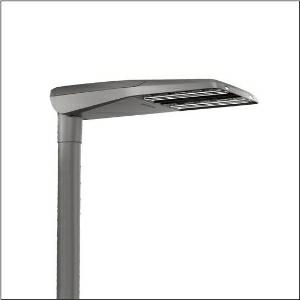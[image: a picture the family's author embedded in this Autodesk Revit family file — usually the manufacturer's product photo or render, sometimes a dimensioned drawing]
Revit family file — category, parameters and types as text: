
# Revit family: streetlight_sl_11_iq_midi___st1_2a_5xc3a51e08le_ac55
name_source: partatom
category: Lighting Fixtures
units: mm (PartAtom-declared; Revit-internal decimal feet)

## family parameters
Cut with Voids When Loaded = No
Host = Face
Light Source = No
Part Type = Normal
Room Calculation Point = No
Round Connector Dimension = Use Diameter
Shared = No

## types (1)
- --- (1 x LED, 9210 lm, 60.4 W, 3000K)
    Apparent Load = 60 VA
    CIE Flux Codes = 32 70 96 100 100
    Color Rendering = 70
    Color Temperature = 3000K
    Default Elevation = 1800 mm
    Description = Streetlight SL 11 iQ midi, mast luminaire, primary light control with 3 zone facetted reflector, of plastic, silver coated, highly specular, primary optical cover: cover, of PMMA, transparent, light distribution: ST1.2a, light emission: direct distribution, primary light characteristic: asymmetric, installation type: post-top, side-entry, lamps: LED, High Power LED, rated values: 9.210lm | 60,4W | 152,5lm/W (begin service life); end service life: 9.210lm | 62,5W; at 50% lumin. flux: 4.605lm | 29,6W | 155,6lm/W, colour temperature: 3000K, colour rendering: CRI > 70, light colour: 730, light setting 1 begin service life: 100% | 9.210lm | 60,4W | 152,5lm/W | 3.000K, light setting 1 end service life: 62,5W, further light settings possible, control: optimised constant luminous flux control (CLO 2.0), Desk-Remote (wireless, voltage-free reading and setting of iQ features in the workshop via application-optimized NFC function/RFID function), Light-Fading, Smart-Wire, Night-Set, Lumen-Switch, Temp-Guard, Auto-Match, with cable H07RN-F 5x 1.5mm², mains connection: 230..240V, AC, 50/60Hz, connection cable pre-assembled, cable length: 8,5m, luminaire housing, of diecast aluminium, powder-coated, Siteco® metallic grey (DB 702S), please order mast flange separately, inclination adjustable without tools: 0°, 5°, 10°, 15° (post-top) | 0°, -5°, -10°, -15° (side-entry), sealing non-destructively replaceable, multi-level sealing system, length: 780mm, width: 376mm, height: 118mm, mast flange for spigot size: 42mm (side-entry): 5XC10008XM4, 60/48mm (side-entry/post-top): 5XC10108XM2, 76/60mm (side-entry/post-top): 5XC10108XM1, equipment: standard, protection rating (complete): IP66, insulation class (complete): insulation class II (safety insulation), certification: CE, ENEC, ENEC+, VDE, impact resistance: IK10, permissible operating ambient temperature for outdoor applications: -25..+50°C, standard-compliant lighting for roads and squares, Environmental Product Declaration (EPD) tested and certified by an independent institute, packaging unit: 1 piece

Light Distribution: ST1.2a
    Height = 118 mm
    Lamp = 1 x LED
    Lamp Light Flux = 9210 lm
    Lamp Power = 60.4 W
    Lamp count = 1
    Length = 780 mm
    Luminous efficacy = 152 lm/W
    Manufacturer = Siteco
    ModVariant = No
    Model = 5XC3A51E08LE
    Number of Poles = 1
    OnlyDefault = Yes
    Power Factor = 1
    Product Name = Streetlight SL 11 iQ midi | ST1.2a
    Product group = mast luminaire | pylon top
    ProductGroupID = 6100
    Protection Class = Protection class II
    Protection Degree = IP 66
    RLX_Detail_Level = 1
    RLX_Emergency_Light_Flux = 0 lm
    RLX_Emergency_Type = 0
    RLX_Emergency_Type_DB = No
    RlxData = <blob elided: 70757 chars, md5=b5577862>
    Socket = socket
    Standby Power = 0 W
    System Light Flux = 9210 lm
    System Power = 60 W
    Type Comments = factory setting: luminous flux: 100 % | dim-lin: 254 | 520 mA
    Type Image = l_1005960.jpg
    URL = http://relux.com
    VarID = @adj_196978
    Voltage = 0 V
    Weight = 0.00 kg
    Width = 376 mm

## geometry (parser evidence)
native form markers: Blend x4, Sweep x9
no freeform markers — native parametric forms only
